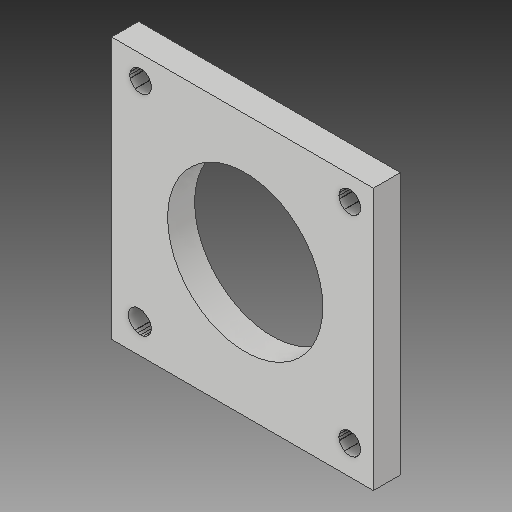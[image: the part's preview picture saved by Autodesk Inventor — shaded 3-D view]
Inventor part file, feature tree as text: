
AUTODESK INVENTOR PART (.ipt)
format: ipt  version: 2018 (Build 220112000, 112)  size: 195,584 bytes
history: native  units: mm
features: other x3, sketch x1
ambient origin geometry x8: Origin, YZ Plane, XZ Plane, XY Plane, X Axis, Y Axis, Z Axis, Center Point
bodies: Solid1 (feature_tree)
feature tree (4):
  other  "F608Brace.ipt"
  other  "Solid1::F608Brace.ipt"
  other  "TaggingFeature1"
  sketch  "Sketch1"  dims[d0=10.0mm]
